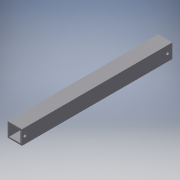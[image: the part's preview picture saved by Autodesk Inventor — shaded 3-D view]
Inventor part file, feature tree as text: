
AUTODESK INVENTOR PART (.ipt)
format: ipt  version: 2018 (Build 220112000, 112)  size: 113,664 bytes
history: native  units: in
note: dims shown in document units (in); Inventor stores cm internally (conversion verified against a paired STEP export)
features: extrude x2, sketch x2
ambient origin geometry x8: Origin, YZ Plane, XZ Plane, XY Plane, X Axis, Y Axis, Z Axis, Center Point
bodies: Solid1 (feature_tree)
feature tree (4):
  extrude  "Extrusion1"  Depth=1.0in
  extrude  "Extrusion2"  Depth=0.1in
  sketch  "Sketch1"  dims[d0=1.0in d1=1.0in]
  sketch  "Sketch2"  dims[d2=0.1in d3=0.1in d4=10.5in d5=0.0in d6=9.878in d7=0.2in d8=0.2in d11=0.1in d12=0.0in d15=0.5in d16=0.5in]
